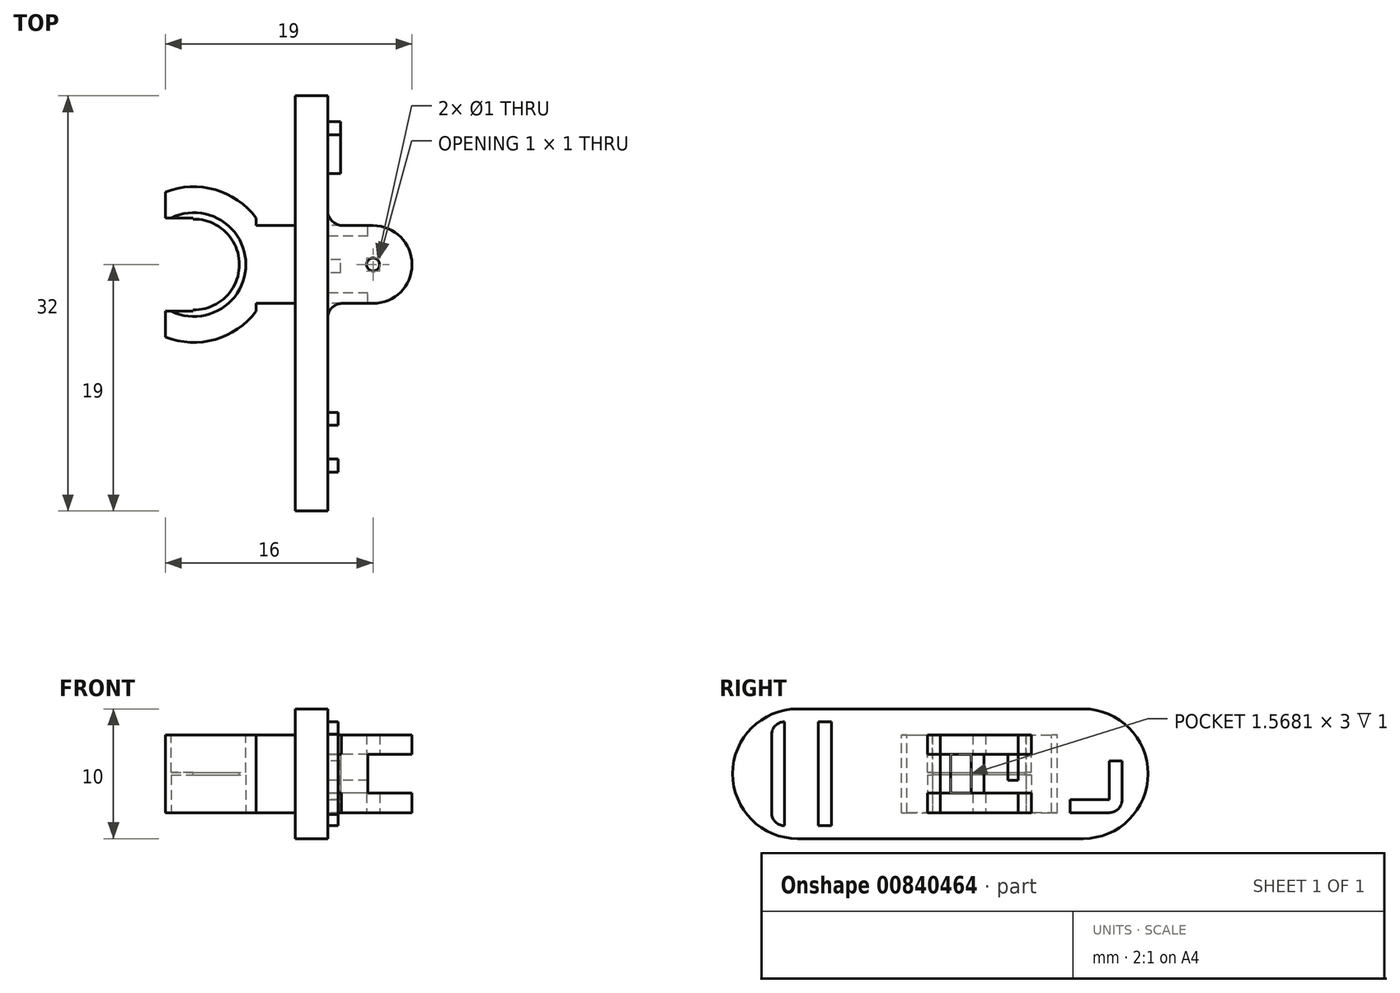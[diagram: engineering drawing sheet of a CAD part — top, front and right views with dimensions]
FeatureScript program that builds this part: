
annotation { "Feature Type Name" : "Feature", "Feature Type Description" : "" }
export const myFeature = defineFeature(function(context is Context, id is Id, definition is map)
    precondition{}
    {
        {
            var Q0;
            Q0=qCreatedBy(makeId("Right.planeOp"),FACE);
            var sketch = newSketch(context, id + "F0", { "sketchPlane" : qUnion([Q0])});
            skLineSegment(sketch, "E0.bottom", {"start": v(-11, 5) * mm, "end": v(11, 5) * mm});
            skLineSegment(sketch, "E0.top", {"start": v(-11, -5) * mm, "end": v(11, -5) * mm});
            skLineSegment(sketch, "E0.left", {"start": v(-16, 0) * mm, "end": v(-16, 0) * mm});
            skLineSegment(sketch, "E0.right", {"start": v(16, 0) * mm, "end": v(16, 0) * mm});
            skPoint(sketch, "E1.visualSharp", {"position": v(-16, 5) * mm});
            skArc(sketch, "E1.filletArc", {"start": v(-11, 5) * mm, "mid": v(-14.54, 3.54) * mm, "end": v(-16, 0) * mm});
            skPoint(sketch, "E2.visualSharp", {"position": v(-16, -5) * mm});
            skArc(sketch, "E2.filletArc", {"start": v(-16, 0) * mm, "mid": v(-14.54, -3.54) * mm, "end": v(-11, -5) * mm});
            skPoint(sketch, "E3.visualSharp", {"position": v(16, 5) * mm});
            skArc(sketch, "E3.filletArc", {"start": v(16, 0) * mm, "mid": v(14.54, 3.54) * mm, "end": v(11, 5) * mm});
            skPoint(sketch, "E4.visualSharp", {"position": v(16, -5) * mm});
            skArc(sketch, "E4.filletArc", {"start": v(11, -5) * mm, "mid": v(14.54, -3.54) * mm, "end": v(16, 0) * mm});
            skSolve(sketch);
        }
        {
            var Q0;
            Q0=makeQuery(id+"F0.imprint","IMPRINT",FACE,{"disambiguationData":[TD([[makeQuery(id+"F0.imprint","IMPRINT",EDGE,{"derivedFrom":sQuery(id+"F0.wireOp",EDGE,"E0.bottom")}),-1.0]])]});
            extrude(context, id + "F1", {"entities" : qUnion([Q0]), "depth" : 2.5 * mm, "offsetDistance" : 25 * mm});
        }
        {
            var Q0;
            Q0=makeQuery(id+"F1.opExtrude","CAP_FACE",FACE,{"disambiguationData":[OSD([sQuery(id+"F0.wireOp",EDGE,"E0.bottom"),sQuery(id+"F0.wireOp",EDGE,"E0.top"),sQuery(id+"F0.wireOp",EDGE,"E1.filletArc"),sQuery(id+"F0.wireOp",EDGE,"E2.filletArc"),sQuery(id+"F0.wireOp",EDGE,"E3.filletArc"),sQuery(id+"F0.wireOp",EDGE,"E4.filletArc")])],"isStart":false});
            var sketch = newSketch(context, id + "F2", { "sketchPlane" : qUnion([Q0])});
            skLineSegment(sketch, "E5", {"start": v(7, 1.5) * mm, "end": v(7, 3) * mm});
            skLineSegment(sketch, "E6", {"start": v(-1, 3) * mm, "end": v(-1, 1.5) * mm});
            skLineSegment(sketch, "E7", {"start": v(7, -3) * mm, "end": v(-1, -3) * mm});
            skLineSegment(sketch, "E8", {"start": v(-1, -3) * mm, "end": v(-1, -1.5) * mm});
            skLineSegment(sketch, "E9", {"start": v(-1, -1.5) * mm, "end": v(7, -1.5) * mm});
            skLineSegment(sketch, "E10", {"start": v(7, -1.5) * mm, "end": v(7, -3) * mm});
            skLineSegment(sketch, "E11", {"start": v(7, 3) * mm, "end": v(-1, 3) * mm});
            skLineSegment(sketch, "E12", {"start": v(-1, 1.5) * mm, "end": v(7, 1.5) * mm});
            skLineSegment(sketch, "E13.trimOffspring", {"start": v(-1, -1.5) * mm, "end": v(-1, -3) * mm});
            skPoint(sketch, "E14.end.orphan", {"position": v(7, -5) * mm});
            skPoint(sketch, "E15.end.orphan", {"position": v(7, 0) * mm});
            skPoint(sketch, "E15.start.orphan", {"position": v(16, 0) * mm});
            skSolve(sketch);
        }
        {
            var Q0;
            Q0 = qSketchRegion(id + "F2", true);
            extrude(context, id + "F3", {"entities" : qUnion([Q0]), "operationType" : NewBodyOperationType.ADD, "depth" : 6.5 * mm, "offsetDistance" : 25 * mm});
        }
        {
            var Q0;
            Q0=makeQuery(id+"F3.opExtrude","SWEPT_FACE",FACE,{"disambiguationData":[OSD([sQuery(id+"F2.wireOp",EDGE,"E7")])]});
            var sketch = newSketch(context, id + "F4", { "sketchPlane" : qUnion([Q0])});
            skLineSegment(sketch, "E16.bottom", {"start": v(2.5, 1) * mm, "end": v(9, 1) * mm});
            skLineSegment(sketch, "E16.top", {"start": v(3.58, 0) * mm, "end": v(6, 0) * mm});
            skLineSegment(sketch, "E16.right", {"start": v(9, 1) * mm, "end": v(9, 0) * mm});
            skLineSegment(sketch, "E17.bottom", {"start": v(2.5, -7) * mm, "end": v(9, -7) * mm});
            skLineSegment(sketch, "E17.top", {"start": v(3.58, -6) * mm, "end": v(6, -6) * mm});
            skLineSegment(sketch, "E17.right", {"start": v(9, -7) * mm, "end": v(9, -6) * mm});
            skArc(sketch, "E18", {"start": v(2.5, 1) * mm, "mid": v(2.85, 0.3) * mm, "end": v(3.58, 0) * mm});
            skArc(sketch, "E19", {"start": v(3.58, -6) * mm, "mid": v(2.88, -6.33) * mm, "end": v(2.5, -7) * mm});
            skArc(sketch, "E20", {"start": v(6, -6) * mm, "mid": v(9, -3) * mm, "end": v(6, 0) * mm});
            skLineSegment(sketch, "E21", {"start": v(9, 0) * mm, "end": v(9, -6) * mm});
            skCircle(sketch, "E22", {"center": v(6, -3) * mm, "radius": 0.5 * mm});
            skSolve(sketch);
        }
        {
            var Q0;
            Q0 = qSketchRegion(id + "F4", true);
            extrude(context, id + "F5", {"entities" : qUnion([Q0]), "operationType" : NewBodyOperationType.REMOVE, "oppositeDirection" : true, "depth" : 25 * mm, "offsetDistance" : 25 * mm});
        }
        {
            var Q0;
            Q0=makeQuery(id+"F1.opExtrude","CAP_FACE",FACE,{"disambiguationData":[OSD([sQuery(id+"F0.wireOp",EDGE,"E0.bottom"),sQuery(id+"F0.wireOp",EDGE,"E0.top"),sQuery(id+"F0.wireOp",EDGE,"E1.filletArc"),sQuery(id+"F0.wireOp",EDGE,"E2.filletArc"),sQuery(id+"F0.wireOp",EDGE,"E3.filletArc"),sQuery(id+"F0.wireOp",EDGE,"E4.filletArc")])],"isStart":false});
            var sketch = newSketch(context, id + "F6", { "sketchPlane" : qUnion([Q0])});
            skLineSegment(sketch, "E23.bottom", {"start": v(0, 1.5) * mm, "end": v(0.8, 1.5) * mm});
            skLineSegment(sketch, "E23.top", {"start": v(0, -1.5) * mm, "end": v(0.8, -1.5) * mm});
            skLineSegment(sketch, "E24.right", {"start": v(5.2, 1.4) * mm, "end": v(5.2, -0.5) * mm});
            skLineSegment(sketch, "E25.bottom", {"start": v(0.8, 1.5) * mm, "end": v(0, 1.5) * mm});
            skLineSegment(sketch, "E25.top", {"start": v(0.8, -1.5) * mm, "end": v(0, -1.5) * mm});
            skLineSegment(sketch, "E25.left", {"start": v(0.8, 1.5) * mm, "end": v(0.8, -1.5) * mm});
            skLineSegment(sketch, "E25.right", {"start": v(0, 1.5) * mm, "end": v(0, -1.5) * mm});
            skPoint(sketch, "E26.orphan", {"position": v(-1, -1.5) * mm});
            skPoint(sketch, "E27.orphan", {"position": v(1, -1.5) * mm});
            skLineSegment(sketch, "E28.right", {"start": v(6, 1.5) * mm, "end": v(6, -0.5) * mm});
            skLineSegment(sketch, "E29.top", {"start": v(5.2, -0.5) * mm, "end": v(6, -0.5) * mm});
            skLineSegment(sketch, "E30.top", {"start": v(5.2, 1.5) * mm, "end": v(6, 1.5) * mm});
            skLineSegment(sketch, "E30.left", {"start": v(5.2, 1.4) * mm, "end": v(5.2, 1.5) * mm});
            skLineSegment(sketch, "E30.right", {"start": v(6, 1.5) * mm, "end": v(6, 1.5) * mm});
            skSolve(sketch);
        }
        {
            var Q0;
            Q0 = qSketchRegion(id + "F6", true);
            extrude(context, id + "F7", {"entities" : qUnion([Q0]), "operationType" : NewBodyOperationType.ADD, "depth" : 3.1 * mm, "offsetDistance" : 25 * mm});
        }
        {
            var Q0;
            Q0=makeQuery(id+"F1.opExtrude","CAP_FACE",FACE,{"disambiguationData":[OSD([sQuery(id+"F0.wireOp",EDGE,"E0.bottom"),sQuery(id+"F0.wireOp",EDGE,"E0.top"),sQuery(id+"F0.wireOp",EDGE,"E1.filletArc"),sQuery(id+"F0.wireOp",EDGE,"E2.filletArc"),sQuery(id+"F0.wireOp",EDGE,"E3.filletArc"),sQuery(id+"F0.wireOp",EDGE,"E4.filletArc")])],"isStart":false});
            var sketch = newSketch(context, id + "F8", { "sketchPlane" : qUnion([Q0])});
            skLineSegment(sketch, "E31.top", {"start": v(13, -2) * mm, "end": v(11, -2) * mm});
            skLineSegment(sketch, "E31.left", {"start": v(13, 0) * mm, "end": v(13, -2) * mm});
            skLineSegment(sketch, "E32.bottom", {"start": v(13, -2) * mm, "end": v(10, -2) * mm});
            skLineSegment(sketch, "E32.top", {"start": v(13, -3) * mm, "end": v(10, -3) * mm});
            skLineSegment(sketch, "E32.right", {"start": v(10, -2) * mm, "end": v(10, -3) * mm});
            skLineSegment(sketch, "E33.top", {"start": v(13, 1) * mm, "end": v(14, 1) * mm});
            skLineSegment(sketch, "E33.left", {"start": v(13, -2) * mm, "end": v(13, 1) * mm});
            skLineSegment(sketch, "E33.right", {"start": v(14, -2.02) * mm, "end": v(14, 1) * mm});
            skPoint(sketch, "E34.start.orphan", {"position": v(16, 0) * mm});
            skArc(sketch, "E35", {"start": v(13, -3) * mm, "mid": v(13.7, -2.71) * mm, "end": v(14, -2.02) * mm});
            skLineSegment(sketch, "E36.bottom", {"start": v(2.37, 1.5) * mm, "end": v(3.37, 1.5) * mm});
            skLineSegment(sketch, "E36.top", {"start": v(2.37, -1.5) * mm, "end": v(3.37, -1.5) * mm});
            skLineSegment(sketch, "E36.left", {"start": v(2.37, 1.5) * mm, "end": v(2.37, -1.5) * mm});
            skLineSegment(sketch, "E36.right", {"start": v(3.37, 1.5) * mm, "end": v(3.37, -1.5) * mm});
            skSolve(sketch);
        }
        {
            var Q0;
            Q0 = qSketchRegion(id + "F8", true);
            extrude(context, id + "F9", {"entities" : qUnion([Q0]), "operationType" : NewBodyOperationType.ADD, "depth" : 1 * mm, "offsetDistance" : 25 * mm});
        }
        {
            var Q0;
            {var subQ0=sQuery(id+"F0.wireOp",EDGE,"E0.top");var subQ1=sQuery(id+"F0.wireOp",EDGE,"E4.filletArc");var subQ2=sQuery(id+"F0.wireOp",EDGE,"E3.filletArc");var subQ3=sQuery(id+"F0.wireOp",EDGE,"E2.filletArc");var subQ4=sQuery(id+"F0.wireOp",EDGE,"E1.filletArc");var subQ5=sQuery(id+"F0.wireOp",EDGE,"E0.bottom");var subQ6=makeQuery(id+"F1.opExtrude","CAP_FACE",FACE,{"disambiguationData":[OSD([subQ5,subQ0,subQ4,subQ3,subQ2,subQ1])],"isStart":false});Q0=makeQuery(id+"F9.boolean.opBoolean","SPLIT",FACE,{"disambiguationData":[TD([makeQuery(id+"F1.opExtrude","SWEPT_FACE",FACE,{"disambiguationData":[OSD([subQ5])]})])],"derivedFrom":subQ6});}
            var sketch = newSketch(context, id + "F10", { "sketchPlane" : qUnion([Q0])});
            skLineSegment(sketch, "E37", {"start": v(-8.9, -4) * mm, "end": v(-9.4, -4) * mm});
            skLineSegment(sketch, "E38", {"start": v(-9.4, 4) * mm, "end": v(-8.9, 4) * mm});
            skPoint(sketch, "E39.orphan", {"position": v(-9.9, 5) * mm});
            skPoint(sketch, "E40.orphan", {"position": v(-9.9, -5) * mm});
            skLineSegment(sketch, "E41", {"start": v(-12, 0) * mm, "end": v(-12, 4) * mm});
            skLineSegment(sketch, "E42", {"start": v(-13, 3.04) * mm, "end": v(-13, -3.13) * mm});
            skLineSegment(sketch, "E43", {"start": v(-12, -4) * mm, "end": v(-12, 0) * mm});
            skArc(sketch, "E44", {"start": v(-12, 4) * mm, "mid": v(-12.7, 3.72) * mm, "end": v(-13, 3.04) * mm});
            skArc(sketch, "E45", {"start": v(-13, -3.13) * mm, "mid": v(-12.66, -3.75) * mm, "end": v(-12, -4) * mm});
            skLineSegment(sketch, "E46.bottom", {"start": v(-8.9, -4) * mm, "end": v(-8.4, -4) * mm});
            skLineSegment(sketch, "E46.top", {"start": v(-8.9, 4) * mm, "end": v(-8.4, 4) * mm});
            skLineSegment(sketch, "E46.right", {"start": v(-8.4, -4) * mm, "end": v(-8.4, 4) * mm});
            skLineSegment(sketch, "E47", {"start": v(-9.4, -4) * mm, "end": v(-9.4, 4) * mm});
            skPoint(sketch, "E48.orphan", {"position": v(-9.9, -4) * mm});
            skPoint(sketch, "E49.orphan", {"position": v(-9.9, 4) * mm});
            skPoint(sketch, "E50.start.orphan", {"position": v(-16, 0) * mm});
            skSolve(sketch);
        }
        {
            var Q0;
            Q0 = qSketchRegion(id + "F10", true);
            extrude(context, id + "F11", {"entities" : qUnion([Q0]), "operationType" : NewBodyOperationType.ADD, "depth" : .8 * mm, "offsetDistance" : 25 * mm});
        }
        {
            var Q0;
            Q0=makeQuery(id+"F1.opExtrude","CAP_FACE",FACE,{"disambiguationData":[OSD([sQuery(id+"F0.wireOp",EDGE,"E0.bottom"),sQuery(id+"F0.wireOp",EDGE,"E0.top"),sQuery(id+"F0.wireOp",EDGE,"E1.filletArc"),sQuery(id+"F0.wireOp",EDGE,"E2.filletArc"),sQuery(id+"F0.wireOp",EDGE,"E3.filletArc"),sQuery(id+"F0.wireOp",EDGE,"E4.filletArc")])],"isStart":true});
            var sketch = newSketch(context, id + "F12", { "sketchPlane" : qUnion([Q0])});
            skLineSegment(sketch, "E51", {"start": v(-6, 0) * mm, "end": v(-6, -3) * mm});
            skLineSegment(sketch, "E52", {"start": v(-6, -3) * mm, "end": v(-6, 3) * mm});
            skLineSegment(sketch, "E53", {"start": v(-6, 3) * mm, "end": v(0, 3) * mm});
            skLineSegment(sketch, "E54", {"start": v(0, 3) * mm, "end": v(0, -3) * mm});
            skLineSegment(sketch, "E55", {"start": v(0, -3) * mm, "end": v(-6, -3) * mm});
            skPoint(sketch, "E56.orphan", {"position": v(-16, 0) * mm});
            skSolve(sketch);
        }
        {
            var Q0;
            Q0 = qSketchRegion(id + "F12", true);
            extrude(context, id + "F13", {"entities" : qUnion([Q0]), "operationType" : NewBodyOperationType.ADD, "depth" : 3 * mm, "offsetDistance" : 25 * mm});
        }
        {
            var Q0;
            Q0=makeQuery(id+"F13.opExtrude","CAP_FACE",FACE,{"disambiguationData":[OSD([sQuery(id+"F12.wireOp",EDGE,"E52"),sQuery(id+"F12.wireOp",EDGE,"E53"),sQuery(id+"F12.wireOp",EDGE,"E54"),sQuery(id+"F12.wireOp",EDGE,"E55")])],"isStart":false});
            var sketch = newSketch(context, id + "F14", { "sketchPlane" : qUnion([Q0])});
            skLineSegment(sketch, "E57", {"start": v(-6, -3) * mm, "end": v(-9, -3) * mm});
            skLineSegment(sketch, "E58", {"start": v(0, 3) * mm, "end": v(3, 3) * mm});
            skLineSegment(sketch, "E59.bottom", {"start": v(3, 3) * mm, "end": v(-9, 3) * mm});
            skLineSegment(sketch, "E59.top", {"start": v(3, -3) * mm, "end": v(-9, -3) * mm});
            skLineSegment(sketch, "E59.left", {"start": v(3, 3) * mm, "end": v(3, -3) * mm});
            skLineSegment(sketch, "E59.right", {"start": v(-9, 3) * mm, "end": v(-9, -3) * mm});
            skSolve(sketch);
        }
        {
            var Q0;
            Q0 = qSketchRegion(id + "F14", true);
            extrude(context, id + "F15", {"entities" : qUnion([Q0]), "operationType" : NewBodyOperationType.ADD, "depth" : 7 * mm, "offsetDistance" : 25 * mm});
        }
        {
            var Q0;
            Q0=makeQuery(id+"F15.boolean.opBoolean","MERGE",FACE,{"derivedFrom":[makeQuery(id+"F13.opExtrude","SWEPT_FACE",FACE,{"disambiguationData":[OSD([sQuery(id+"F12.wireOp",EDGE,"E55")])]}),makeQuery(id+"F15.opExtrude","SWEPT_FACE",FACE,{"disambiguationData":[OSD([sQuery(id+"F14.wireOp",EDGE,"E59.top")])]})]});
            var sketch = newSketch(context, id + "F16", { "sketchPlane" : qUnion([Q0])});
            skCircle(sketch, "E60", {"center": v(-7.8, -3) * mm, "radius": 4 * mm});
            skPoint(sketch, "E61.orphan", {"position": v(-10, -3) * mm});
            skPoint(sketch, "E62.start.orphan", {"position": v(0, -3) * mm});
            skSolve(sketch);
        }
        {
            var Q0;
            Q0 = qSketchRegion(id + "F16", true);
            extrude(context, id + "F17", {"entities" : qUnion([Q0]), "operationType" : NewBodyOperationType.REMOVE, "oppositeDirection" : true, "depth" : 2.9 * mm, "offsetDistance" : 25 * mm});
        }
        {
            var Q0;
            Q0=makeQuery(id+"F15.boolean.opBoolean","MERGE",FACE,{"derivedFrom":[makeQuery(id+"F13.opExtrude","SWEPT_FACE",FACE,{"disambiguationData":[OSD([sQuery(id+"F12.wireOp",EDGE,"E53")])]}),makeQuery(id+"F15.opExtrude","SWEPT_FACE",FACE,{"disambiguationData":[OSD([sQuery(id+"F14.wireOp",EDGE,"E59.bottom")])]})]});
            var sketch = newSketch(context, id + "F18", { "sketchPlane" : qUnion([Q0])});
            skCircle(sketch, "E63", {"center": v(-7.8, 3) * mm, "radius": 4 * mm});
            skPoint(sketch, "E64.start.orphan", {"position": v(0, 3) * mm});
            skSolve(sketch);
        }
        {
            var Q0;
            Q0 = qSketchRegion(id + "F18", true);
            extrude(context, id + "F19", {"entities" : qUnion([Q0]), "operationType" : NewBodyOperationType.REMOVE, "oppositeDirection" : true, "depth" : 2.9 * mm, "offsetDistance" : 25 * mm});
        }
        {
            var Q0;
            Q0=makeQuery(id+"F19.boolean.opBoolean","COPY",FACE,{"derivedFrom":makeQuery(id+"F19.opExtrude","CAP_FACE",FACE,{"disambiguationData":[OSD([sQuery(id+"F18.wireOp",EDGE,"E63")])],"isStart":false})});
            var sketch = newSketch(context, id + "F20", { "sketchPlane" : qUnion([Q0])});
            skLineSegment(sketch, "E65", {"start": v(-3.8, 3) * mm, "end": v(-7.8, 3) * mm});
            skCircle(sketch, "E66", {"center": v(-7.8, 3) * mm, "radius": 3.5 * mm});
            skSolve(sketch);
        }
        {
            var Q0;
            Q0 = qSketchRegion(id + "F20", true);
            extrude(context, id + "F21", {"entities" : qUnion([Q0]), "operationType" : NewBodyOperationType.REMOVE, "oppositeDirection" : true, "depth" : 25 * mm, "offsetDistance" : 25 * mm});
        }
        {
            var Q0;
            Q0=makeQuery(id+"F15.boolean.opBoolean","MERGE",FACE,{"derivedFrom":[makeQuery(id+"F13.opExtrude","SWEPT_FACE",FACE,{"disambiguationData":[OSD([sQuery(id+"F12.wireOp",EDGE,"E53")])]}),makeQuery(id+"F15.opExtrude","SWEPT_FACE",FACE,{"disambiguationData":[OSD([sQuery(id+"F14.wireOp",EDGE,"E59.bottom")])]})]});
            var sketch = newSketch(context, id + "F22", { "sketchPlane" : qUnion([Q0])});
            skArc(sketch, "E67", {"start": v(-3, 6.6) * mm, "mid": v(-7.8, 9) * mm, "end": v(-12.6, 6.6) * mm});
            skLineSegment(sketch, "E68", {"start": v(-3, 6.6) * mm, "end": v(-3, 10.6) * mm});
            skLineSegment(sketch, "E69", {"start": v(-3, -0.6) * mm, "end": v(-3, -4.6) * mm});
            skLineSegment(sketch, "E70", {"start": v(-3, -4.6) * mm, "end": v(-18.03, -4.6) * mm});
            skLineSegment(sketch, "E71.bottom", {"start": v(-18.03, -4.6) * mm, "end": v(-3, -4.6) * mm});
            skLineSegment(sketch, "E71.top", {"start": v(-18.03, 10.6) * mm, "end": v(-3, 10.6) * mm});
            skLineSegment(sketch, "E71.left", {"start": v(-18.03, -4.6) * mm, "end": v(-18.03, 10.6) * mm});
            skLineSegment(sketch, "E71.right", {"start": v(-3, -4.6) * mm, "end": v(-3, -0.6) * mm});
            skLineSegment(sketch, "E72", {"start": v(-7.87, 6.6) * mm, "end": v(-7.87, -0.6) * mm});
            skPoint(sketch, "E73.orphan", {"position": v(-11.26, -0.6) * mm});
            skLineSegment(sketch, "E74", {"start": v(-7.87, 6.6) * mm, "end": v(-12.6, 6.6) * mm});
            skLineSegment(sketch, "E75", {"start": v(-7.87, -0.6) * mm, "end": v(-12.6, -0.6) * mm});
            skPoint(sketch, "E76.start.orphan", {"position": v(-3.8, 3) * mm});
            skArc(sketch, "E77.trimOffspring", {"start": v(-12.6, -0.6) * mm, "mid": v(-7.8, -3) * mm, "end": v(-3, -0.6) * mm});
            skSolve(sketch);
        }
        {
            var Q0;
            Q0 = qSketchRegion(id + "F22", true);
            extrude(context, id + "F23", {"entities" : qUnion([Q0]), "operationType" : NewBodyOperationType.REMOVE, "oppositeDirection" : true, "depth" : 25 * mm, "offsetDistance" : 25 * mm});
        }
    });
